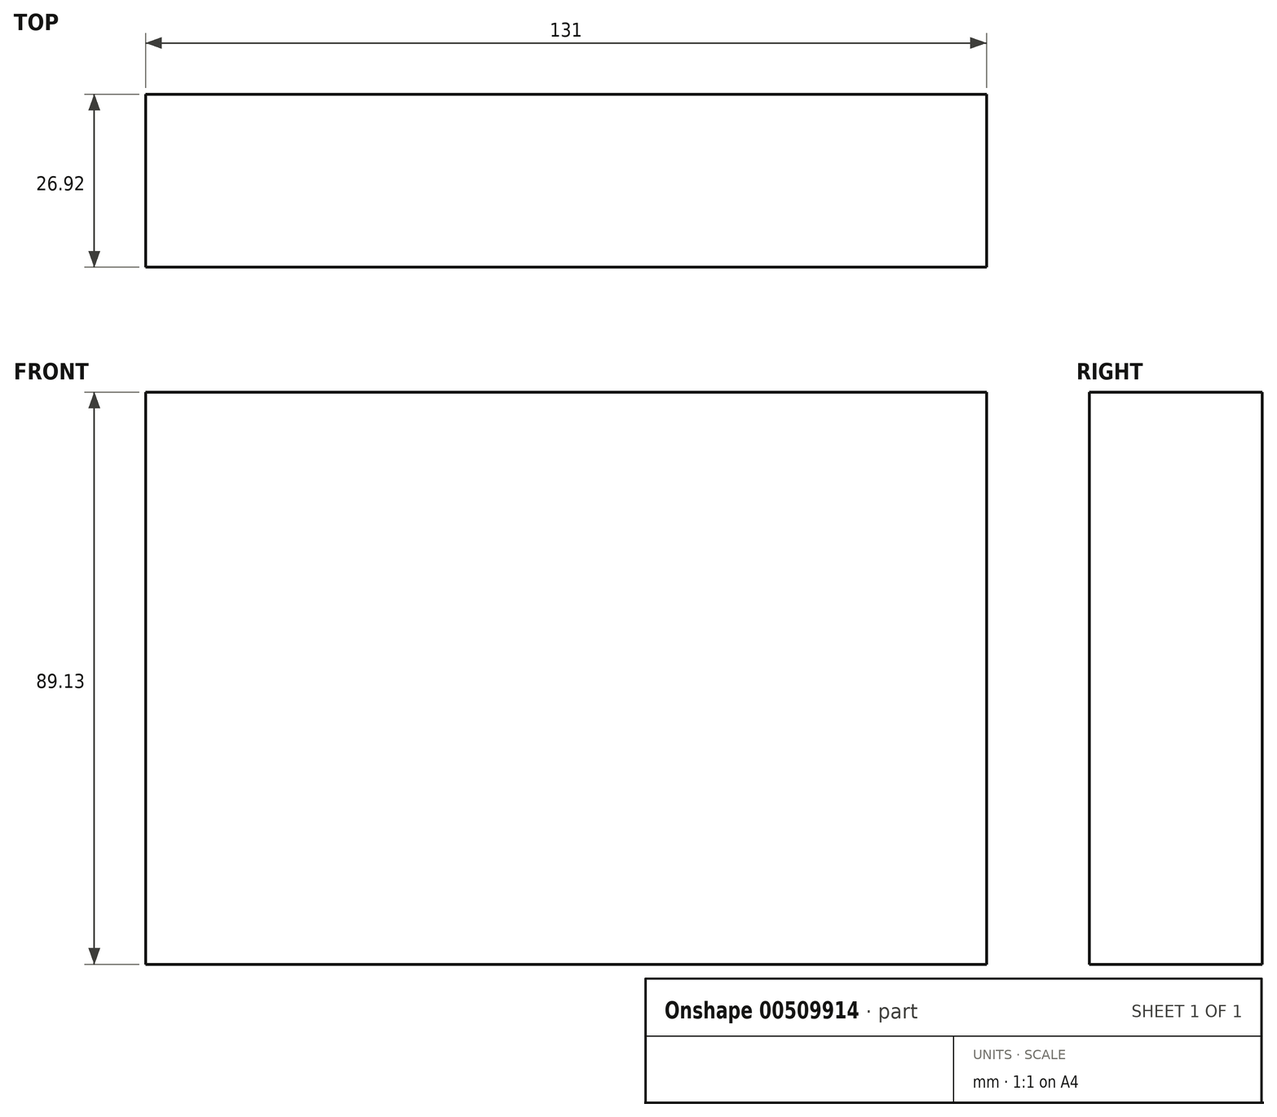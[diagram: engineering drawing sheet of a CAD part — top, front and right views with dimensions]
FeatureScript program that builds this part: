
annotation { "Feature Type Name" : "Feature", "Feature Type Description" : "" }
export const myFeature = defineFeature(function(context is Context, id is Id, definition is map)
    precondition{}
    {
        {
            var Q0;
            Q0=qCreatedBy(makeId("Front.planeOp"),FACE);
            var sketch = newSketch(context, id + "F0", { "sketchPlane" : qUnion([Q0])});
            skLineSegment(sketch, "E0.bottom", {"start": v(0, 0) * mm, "end": v(131, 0) * mm});
            skLineSegment(sketch, "E0.top", {"start": v(0, 89.13) * mm, "end": v(131, 89.13) * mm});
            skLineSegment(sketch, "E0.left", {"start": v(0, 0) * mm, "end": v(0, 89.13) * mm});
            skLineSegment(sketch, "E0.right", {"start": v(131, 0) * mm, "end": v(131, 89.13) * mm});
            skSolve(sketch);
        }
        {
            var Q0;
            Q0=makeQuery(id+"F0.imprint","IMPRINT",FACE,{"disambiguationData":[TD([[makeQuery(id+"F0.imprint","IMPRINT",EDGE,{"derivedFrom":sQuery(id+"F0.wireOp",EDGE,"E0.bottom")}),1.0]])]});
            extrude(context, id + "F1", {"entities" : qUnion([Q0]), "depth" : 26.92 * mm});
        }
    });
